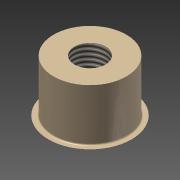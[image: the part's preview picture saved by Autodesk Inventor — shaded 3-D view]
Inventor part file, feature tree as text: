
AUTODESK INVENTOR PART (.ipt)
format: ipt  version: 2015 (Build 190159000, 159)  size: 131,584 bytes
history: native  units: mm
features: sketch x2, other x1, extrude x1, shell x1, revolve x1, fillet x1, thread x1
ambient origin geometry x8: Origin, YZ Plane, XZ Plane, XY Plane, X Axis, Y Axis, Z Axis, Center Point
bodies: Body1 (feature_tree)
feature tree (8):
  other  "Bryła1"
  extrude  "Wyciągnięcie proste1"  Depth=28.0mm
  shell  "Skorupa1"  Thickness=20.0mm
  revolve  "Obrót1"
  fillet  "Zaokrąglenie1"  Radius=8.0mm
  thread  "Gwint1"
  sketch  "Szkic1"
  sketch  "Szkic2"
